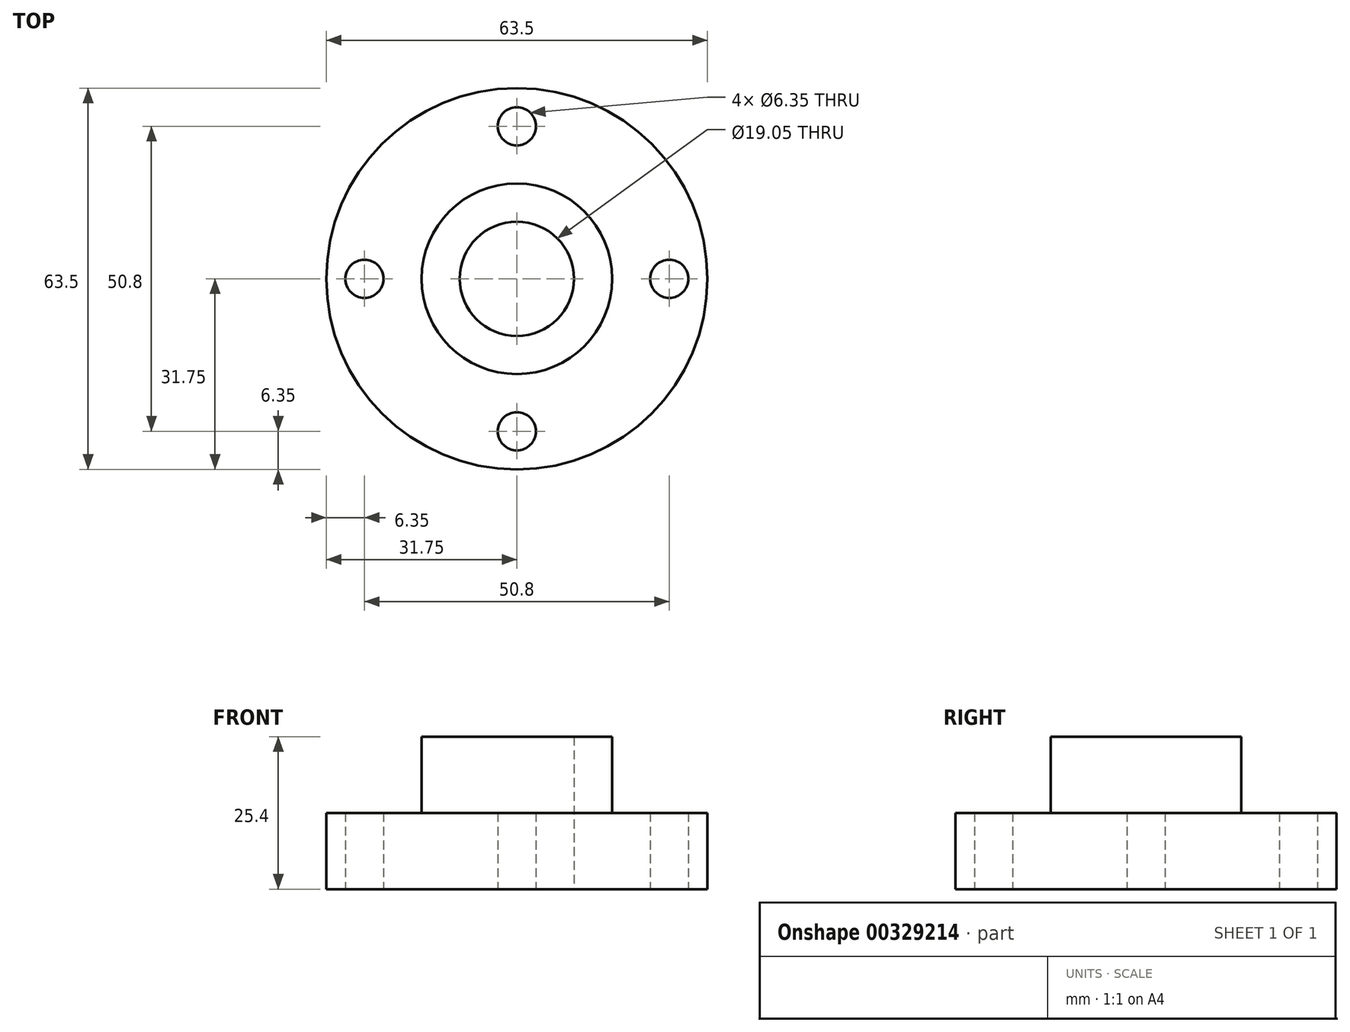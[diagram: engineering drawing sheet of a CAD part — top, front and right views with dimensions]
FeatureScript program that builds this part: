
annotation { "Feature Type Name" : "Feature", "Feature Type Description" : "" }
export const myFeature = defineFeature(function(context is Context, id is Id, definition is map)
    precondition{}
    {
        {
            var Q0;
            Q0=qCreatedBy(makeId("Top.planeOp"),FACE);
            var sketch = newSketch(context, id + "F0", { "sketchPlane" : qUnion([Q0])});
            skCircle(sketch, "E0", {"center": v(0, 0) * mm, "radius": 31.75 * mm});
            skCircle(sketch, "E1", {"center": v(0, 0) * mm, "radius": 25.4 * mm, "construction": true});
            skCircle(sketch, "E2", {"center": v(0, 0) * mm, "radius": 15.88 * mm});
            skCircle(sketch, "E3", {"center": v(0, 0) * mm, "radius": 9.53 * mm});
            skCircle(sketch, "E4", {"center": v(0, 25.4) * mm, "radius": 3.18 * mm});
            skCircle(sketch, "E5", {"center": v(-25.4, 0) * mm, "radius": 3.18 * mm});
            skCircle(sketch, "E6", {"center": v(25.4, 0) * mm, "radius": 3.18 * mm});
            skCircle(sketch, "E7", {"center": v(0, -25.4) * mm, "radius": 3.18 * mm});
            skSolve(sketch);
        }
        {
            var Q0;
            Q0=makeQuery(id+"F0.imprint","IMPRINT",FACE,{"disambiguationData":[TD([[makeQuery(id+"F0.imprint","IMPRINT",EDGE,{"derivedFrom":sQuery(id+"F0.wireOp",EDGE,"E2")}),1.0]])]});
            extrude(context, id + "F1", {"entities" : qUnion([Q0]), "depth" : 25.4 * mm});
        }
        {
            var Q0;
            Q0=makeQuery(id+"F0.imprint","IMPRINT",FACE,{"disambiguationData":[TD([[makeQuery(id+"F0.imprint","IMPRINT",EDGE,{"derivedFrom":sQuery(id+"F0.wireOp",EDGE,"E0")}),1.0]])]});
            extrude(context, id + "F2", {"entities" : qUnion([Q0]), "operationType" : NewBodyOperationType.ADD, "depth" : 12.7 * mm});
        }
    });
